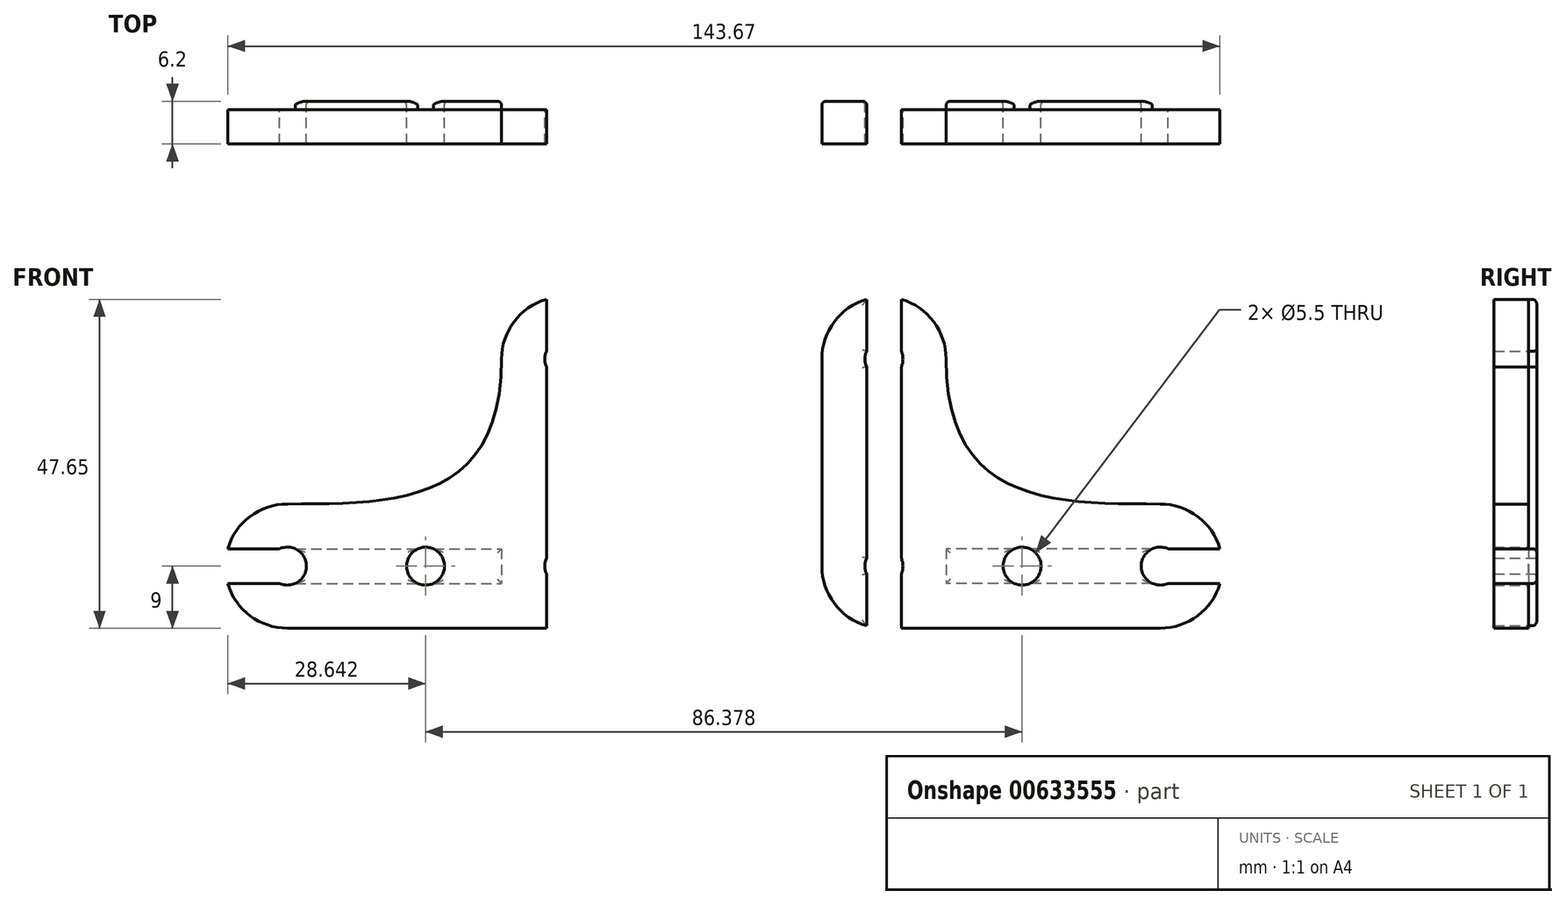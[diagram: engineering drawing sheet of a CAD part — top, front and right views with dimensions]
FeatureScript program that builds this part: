
annotation { "Feature Type Name" : "Feature", "Feature Type Description" : "" }
export const myFeature = defineFeature(function(context is Context, id is Id, definition is map)
    precondition{}
    {
        {
            var Q0;
            Q0=qCreatedBy(makeId("Front.planeOp"),FACE);
            var sketch = newSketch(context, id + "F0", { "sketchPlane" : qUnion([Q0])});
            skLineSegment(sketch, "E0.left", {"start": v(-18, 0) * mm, "end": v(-18, 30) * mm});
            skArc(sketch, "E1", {"start": v(-18, 30) * mm, "mid": v(-9, 39) * mm, "end": v(0, 30) * mm});
            skArc(sketch, "E2", {"start": v(31, 9) * mm, "mid": v(37.36, 6.36) * mm, "end": v(40, 0) * mm});
            skLineSegment(sketch, "E3", {"start": v(0, 30) * mm, "end": v(0, 9) * mm, "construction": true});
            skLineSegment(sketch, "E4", {"start": v(0, 9) * mm, "end": v(31, 9) * mm, "construction": true});
            skLineSegment(sketch, "E5", {"start": v(-18, 39) * mm, "end": v(0, 39) * mm, "construction": true});
            skFitSpline(sketch, "E6", {"points": [v(0, 30) * mm, v(31, 9) * mm], "startDerivative": vector(0, -63) * mm, "endDerivative": vector(46.5, 0) * mm});
            skCircle(sketch, "E7", {"center": v(-9, 30) * mm, "radius": 2.75 * mm});
            skCircle(sketch, "E8", {"center": v(-9, 0) * mm, "radius": 2.75 * mm});
            skCircle(sketch, "E9", {"center": v(31, 0) * mm, "radius": 2.75 * mm});
            skCircle(sketch, "E10", {"center": v(11, 0) * mm, "radius": 2.75 * mm});
            skLineSegment(sketch, "E11.MirrorCS", {"start": v(-18, 0) * mm, "end": v(-18, 0) * mm});
            skArc(sketch, "E12.MirrorCS", {"start": v(31, -9) * mm, "mid": v(37.36, -6.36) * mm, "end": v(40, 0) * mm});
            skCircle(sketch, "E13", {"center": v(-9, 30) * mm, "radius": 2.5 * mm, "construction": true});
            skCircle(sketch, "E14", {"center": v(31, 0) * mm, "radius": 2.5 * mm, "construction": true});
            skLineSegment(sketch, "E15.left", {"start": v(-6.5, 38.65) * mm, "end": v(-6.5, -9) * mm});
            skLineSegment(sketch, "E16.bottom", {"start": v(39.65, 2.5) * mm, "end": v(0, 2.5) * mm});
            skLineSegment(sketch, "E16.top", {"start": v(39.65, -2.5) * mm, "end": v(0, -2.5) * mm});
            skLineSegment(sketch, "E16.right", {"start": v(0, 2.5) * mm, "end": v(0, -2.5) * mm});
            skPoint(sketch, "E16.middle", {"position": v(19.82, 0) * mm});
            skLineSegment(sketch, "E17", {"start": v(31, -9) * mm, "end": v(-9, -9) * mm});
            skPoint(sketch, "E18.orphan", {"position": v(-11.5, -38.65) * mm});
            skPoint(sketch, "E19.orphan", {"position": v(-6.5, -38.65) * mm});
            skArc(sketch, "E20.filletArc", {"start": v(-18, 0) * mm, "mid": v(-15.36, -6.36) * mm, "end": v(-9, -9) * mm});
            skLineSegment(sketch, "E21", {"start": v(-11.5, 38.65) * mm, "end": v(-11.5, -8.65) * mm});
            skLineSegment(sketch, "E22", {"start": v(-32.19, 44.68) * mm, "end": v(-32.19, -13.7) * mm});
            skSolve(sketch);
        }
        {
            var Q0;
            {var subQ0=sQuery(id+"F0.wireOp",EDGE,"E15.right");var subQ1=sQuery(id+"F0.wireOp",EDGE,"E8");var subQ2=makeQuery(id+"F0.imprint","INTERSECT",VERTEX,{"disambiguationData":[OD(1.0)],"derivedFrom":[subQ1,subQ0]});Q0=makeQuery(id+"F0.imprint","IMPRINT",FACE,{"disambiguationData":[TD([[makeQuery(id+"F0.imprint","IMPRINT",EDGE,{"disambiguationData":[TD([[subQ2,-1.0]])],"derivedFrom":subQ1}),-1.0]])]});}
            var Q1;
            {var subQ12=sQuery(id+"F0.wireOp",EDGE,"E0.left");Q1=makeQuery(id+"F0.imprint","IMPRINT",FACE,{"disambiguationData":[TD([[makeQuery(id+"F0.imprint","IMPRINT",EDGE,{"derivedFrom":subQ12}),-1.0]])]});}
            var Q2;
            {var subQ0=sQuery(id+"F0.wireOp",EDGE,"E16.bottom");var subQ1=sQuery(id+"F0.wireOp",EDGE,"E9");var subQ2=makeQuery(id+"F0.imprint","INTERSECT",VERTEX,{"disambiguationData":[OD(0.0)],"derivedFrom":[subQ1,subQ0]});Q2=makeQuery(id+"F0.imprint","IMPRINT",FACE,{"disambiguationData":[TD([[makeQuery(id+"F0.imprint","IMPRINT",EDGE,{"disambiguationData":[TD([[subQ2,-1.0]])],"derivedFrom":subQ1}),-1.0]])]});}
            var Q3;
            {var subQ0=sQuery(id+"F0.wireOp",EDGE,"E15.right");var subQ1=sQuery(id+"F0.wireOp",EDGE,"807e0331-1f37-435d-b5e4-c923ac2277230.MirrorC");var subQ2=makeQuery(id+"F0.imprint","INTERSECT",VERTEX,{"disambiguationData":[OD(0.0)],"derivedFrom":[subQ1,subQ0]});Q3=makeQuery(id+"F0.imprint","IMPRINT",FACE,{"disambiguationData":[TD([[makeQuery(id+"F0.imprint","IMPRINT",EDGE,{"disambiguationData":[TD([[subQ2,1.0]])],"derivedFrom":subQ1}),-1.0]])]});}
            var Q4;
            {var subQ0=sQuery(id+"F0.wireOp",EDGE,"E15.right");var subQ1=sQuery(id+"F0.wireOp",EDGE,"E7");var subQ2=makeQuery(id+"F0.imprint","INTERSECT",VERTEX,{"disambiguationData":[OD(0.0)],"derivedFrom":[subQ1,subQ0]});Q4=makeQuery(id+"F0.imprint","IMPRINT",FACE,{"disambiguationData":[TD([[makeQuery(id+"F0.imprint","IMPRINT",EDGE,{"disambiguationData":[TD([[subQ2,1.0]])],"derivedFrom":subQ1}),1.0]])]});}
            var Q5;
            {var subQ0=sQuery(id+"F0.wireOp",EDGE,"E15.right");var subQ1=sQuery(id+"F0.wireOp",EDGE,"E8");var subQ2=makeQuery(id+"F0.imprint","INTERSECT",VERTEX,{"disambiguationData":[OD(0.0)],"derivedFrom":[subQ1,subQ0]});Q5=makeQuery(id+"F0.imprint","IMPRINT",FACE,{"disambiguationData":[TD([[makeQuery(id+"F0.imprint","IMPRINT",EDGE,{"disambiguationData":[TD([[subQ2,1.0]])],"derivedFrom":subQ1}),1.0]])]});}
            var Q6;
            {var subQ0=sQuery(id+"F0.wireOp",EDGE,"E15.right");var subQ1=sQuery(id+"F0.wireOp",EDGE,"E7");var subQ2=makeQuery(id+"F0.imprint","INTERSECT",VERTEX,{"disambiguationData":[OD(1.0)],"derivedFrom":[subQ1,subQ0]});Q6=makeQuery(id+"F0.imprint","IMPRINT",FACE,{"disambiguationData":[TD([[makeQuery(id+"F0.imprint","IMPRINT",EDGE,{"disambiguationData":[TD([[subQ2,-1.0]])],"derivedFrom":subQ1}),-1.0]])]});}
            var Q7;
            {var subQ5=sQuery(id+"F0.wireOp",EDGE,"E16.right");Q7=makeQuery(id+"F0.imprint","IMPRINT",FACE,{"disambiguationData":[TD([[makeQuery(id+"F0.imprint","IMPRINT",EDGE,{"derivedFrom":subQ5}),1.0]])]});}
            var Q8;
            {var subQ0=sQuery(id+"F0.wireOp",EDGE,"E15.right");var subQ1=sQuery(id+"F0.wireOp",EDGE,"E8");var subQ2=makeQuery(id+"F0.imprint","INTERSECT",VERTEX,{"disambiguationData":[OD(0.0)],"derivedFrom":[subQ1,subQ0]});Q8=makeQuery(id+"F0.imprint","IMPRINT",FACE,{"disambiguationData":[TD([[makeQuery(id+"F0.imprint","IMPRINT",EDGE,{"disambiguationData":[TD([[subQ2,-1.0]])],"derivedFrom":subQ1}),1.0]])]});}
            var Q9;
            {var subQ0=sQuery(id+"F0.wireOp",EDGE,"E15.left");var subQ1=sQuery(id+"F0.wireOp",EDGE,"62d9e975-9eb4-4a92-8864-7b3c9c0b367b0.MirrorCS");var subQ2=makeQuery(id+"F0.imprint","INTERSECT",VERTEX,{"derivedFrom":[subQ1,subQ0]});Q9=makeQuery(id+"F0.imprint","IMPRINT",FACE,{"disambiguationData":[TD([[makeQuery(id+"F0.imprint","IMPRINT",EDGE,{"disambiguationData":[TD([[subQ2,1.0]])],"derivedFrom":subQ1}),1.0]])]});}
            var Q10;
            {var subQ21=sQuery(id+"F0.wireOp",EDGE,"E6");Q10=makeQuery(id+"F0.imprint","IMPRINT",FACE,{"disambiguationData":[TD([[makeQuery(id+"F0.imprint","IMPRINT",EDGE,{"derivedFrom":subQ21}),-1.0]])]});}
            var Q11;
            {var subQ1=sQuery(id+"F0.wireOp",EDGE,"E2");var subQ5=sQuery(id+"F0.wireOp",EDGE,"E12.MirrorCS");var subQ6=makeQuery(id+"F0.imprint","INTERSECT",VERTEX,{"derivedFrom":[subQ1,subQ5]});Q11=makeQuery(id+"F0.imprint","IMPRINT",FACE,{"disambiguationData":[TD([[makeQuery(id+"F0.imprint","IMPRINT",EDGE,{"disambiguationData":[TD([[subQ6,1.0]])],"derivedFrom":subQ1}),-1.0]])]});}
            var Q12;
            {var subQ0=sQuery(id+"F0.wireOp",EDGE,"E15.left");var subQ1=sQuery(id+"F0.wireOp",EDGE,"E1");var subQ2=makeQuery(id+"F0.imprint","INTERSECT",VERTEX,{"derivedFrom":[subQ1,subQ0]});Q12=makeQuery(id+"F0.imprint","IMPRINT",FACE,{"disambiguationData":[TD([[makeQuery(id+"F0.imprint","IMPRINT",EDGE,{"disambiguationData":[TD([[subQ2,1.0]])],"derivedFrom":subQ1}),-1.0]])]});}
            var Q13;
            {var subQ0=sQuery(id+"F0.wireOp",EDGE,"E15.left");var subQ1=sQuery(id+"F0.wireOp",EDGE,"807e0331-1f37-435d-b5e4-c923ac2277230.MirrorC");var subQ2=makeQuery(id+"F0.imprint","INTERSECT",VERTEX,{"disambiguationData":[OD(0.0)],"derivedFrom":[subQ1,subQ0]});Q13=makeQuery(id+"F0.imprint","IMPRINT",FACE,{"disambiguationData":[TD([[makeQuery(id+"F0.imprint","IMPRINT",EDGE,{"disambiguationData":[TD([[subQ2,1.0]])],"derivedFrom":subQ1}),-1.0]])]});}
            var Q14;
            {var subQ0=sQuery(id+"F0.wireOp",EDGE,"E15.right");var subQ1=sQuery(id+"F0.wireOp",EDGE,"E7");var subQ2=makeQuery(id+"F0.imprint","INTERSECT",VERTEX,{"disambiguationData":[OD(0.0)],"derivedFrom":[subQ1,subQ0]});Q14=makeQuery(id+"F0.imprint","IMPRINT",FACE,{"disambiguationData":[TD([[makeQuery(id+"F0.imprint","IMPRINT",EDGE,{"disambiguationData":[TD([[subQ2,-1.0]])],"derivedFrom":subQ1}),1.0]])]});}
            var Q15;
            {var subQ0=sQuery(id+"F0.wireOp",EDGE,"E15.right");var subQ1=sQuery(id+"F0.wireOp",EDGE,"807e0331-1f37-435d-b5e4-c923ac2277230.MirrorC");var subQ2=makeQuery(id+"F0.imprint","INTERSECT",VERTEX,{"disambiguationData":[OD(0.0)],"derivedFrom":[subQ1,subQ0]});Q15=makeQuery(id+"F0.imprint","IMPRINT",FACE,{"disambiguationData":[TD([[makeQuery(id+"F0.imprint","IMPRINT",EDGE,{"disambiguationData":[TD([[subQ2,-1.0]])],"derivedFrom":subQ1}),-1.0]])]});}
            var Q16;
            {var subQ0=sQuery(id+"F0.wireOp",EDGE,"E21");var subQ1=sQuery(id+"F0.wireOp",EDGE,"E7");var subQ2=makeQuery(id+"F0.imprint","INTERSECT",VERTEX,{"disambiguationData":[OD(1.0)],"derivedFrom":[subQ1,subQ0]});Q16=makeQuery(id+"F0.imprint","IMPRINT",FACE,{"disambiguationData":[TD([[makeQuery(id+"F0.imprint","IMPRINT",EDGE,{"disambiguationData":[TD([[subQ2,-1.0]])],"derivedFrom":subQ1}),-1.0]])]});}
            var Q17;
            {var subQ5=sQuery(id+"F0.wireOp",EDGE,"E21");var subQ7=sQuery(id+"F0.wireOp",EDGE,"E8");var subQ9=makeQuery(id+"F0.imprint","INTERSECT",VERTEX,{"disambiguationData":[OD(1.0)],"derivedFrom":[subQ7,subQ5]});Q17=makeQuery(id+"F0.imprint","IMPRINT",FACE,{"disambiguationData":[TD([[makeQuery(id+"F0.imprint","IMPRINT",EDGE,{"disambiguationData":[TD([[subQ9,-1.0]])],"derivedFrom":subQ7}),-1.0]])]});}
            extrude(context, id + "F1", {"entities" : qUnion([Q0, Q1, Q2, Q3, Q4, Q5, Q6, Q7, Q8, Q9, Q10, Q11, Q12, Q13, Q14, Q15, Q16, Q17]), "depth" : 5 * mm, "offsetDistance" : 25 * mm});
        }
        {
            var Q0;
            {var subQ3=sQuery(id+"F0.wireOp",EDGE,"E8");var subQ6=sQuery(id+"F0.wireOp",EDGE,"E15.right");var subQ8=makeQuery(id+"F0.imprint","INTERSECT",VERTEX,{"disambiguationData":[OD(1.0)],"derivedFrom":[subQ3,subQ6]});Q0=makeQuery(id+"F0.imprint","IMPRINT",FACE,{"disambiguationData":[TD([[makeQuery(id+"F0.imprint","IMPRINT",EDGE,{"disambiguationData":[TD([[subQ8,-1.0]])],"derivedFrom":subQ3}),-1.0]])]});}
            var Q1;
            {var subQ3=sQuery(id+"F0.wireOp",EDGE,"E8");var subQ6=sQuery(id+"F0.wireOp",EDGE,"E15.right");var subQ8=makeQuery(id+"F0.imprint","INTERSECT",VERTEX,{"disambiguationData":[OD(0.0)],"derivedFrom":[subQ3,subQ6]});Q1=makeQuery(id+"F0.imprint","IMPRINT",FACE,{"disambiguationData":[TD([[makeQuery(id+"F0.imprint","IMPRINT",EDGE,{"disambiguationData":[TD([[subQ8,1.0]])],"derivedFrom":subQ3}),-1.0]])]});}
            var Q2;
            {var subQ5=sQuery(id+"F0.wireOp",EDGE,"E16.right");Q2=makeQuery(id+"F0.imprint","IMPRINT",FACE,{"disambiguationData":[TD([[makeQuery(id+"F0.imprint","IMPRINT",EDGE,{"derivedFrom":subQ5}),1.0]])]});}
            var Q3;
            {var subQ1=sQuery(id+"F0.wireOp",EDGE,"E16.bottom");var subQ4=sQuery(id+"F0.wireOp",EDGE,"E10");var subQ5=makeQuery(id+"F0.imprint","INTERSECT",VERTEX,{"disambiguationData":[OD(1.0)],"derivedFrom":[subQ4,subQ1]});Q3=makeQuery(id+"F0.imprint","IMPRINT",FACE,{"disambiguationData":[TD([[makeQuery(id+"F0.imprint","IMPRINT",EDGE,{"disambiguationData":[TD([[subQ5,1.0]])],"derivedFrom":subQ4}),-1.0]])]});}
            var Q4;
            {var subQ1=sQuery(id+"F0.wireOp",EDGE,"E2");var subQ5=sQuery(id+"F0.wireOp",EDGE,"E12.MirrorCS");var subQ6=makeQuery(id+"F0.imprint","INTERSECT",VERTEX,{"derivedFrom":[subQ1,subQ5]});Q4=makeQuery(id+"F0.imprint","IMPRINT",FACE,{"disambiguationData":[TD([[makeQuery(id+"F0.imprint","IMPRINT",EDGE,{"disambiguationData":[TD([[subQ6,1.0]])],"derivedFrom":subQ1}),-1.0]])]});}
            var Q5;
            {var subQ0=sQuery(id+"F0.wireOp",EDGE,"E15.left");var subQ1=sQuery(id+"F0.wireOp",EDGE,"E1");var subQ2=makeQuery(id+"F0.imprint","INTERSECT",VERTEX,{"derivedFrom":[subQ1,subQ0]});Q5=makeQuery(id+"F0.imprint","IMPRINT",FACE,{"disambiguationData":[TD([[makeQuery(id+"F0.imprint","IMPRINT",EDGE,{"disambiguationData":[TD([[subQ2,1.0]])],"derivedFrom":subQ1}),-1.0]])]});}
            var Q6;
            {var subQ0=sQuery(id+"F0.wireOp",EDGE,"E15.left");var subQ1=sQuery(id+"F0.wireOp",EDGE,"62d9e975-9eb4-4a92-8864-7b3c9c0b367b0.MirrorCS");var subQ2=makeQuery(id+"F0.imprint","INTERSECT",VERTEX,{"derivedFrom":[subQ1,subQ0]});Q6=makeQuery(id+"F0.imprint","IMPRINT",FACE,{"disambiguationData":[TD([[makeQuery(id+"F0.imprint","IMPRINT",EDGE,{"disambiguationData":[TD([[subQ2,1.0]])],"derivedFrom":subQ1}),1.0]])]});}
            var Q7;
            {var subQ0=sQuery(id+"F0.wireOp",EDGE,"E21");var subQ1=sQuery(id+"F0.wireOp",EDGE,"E7");var subQ2=makeQuery(id+"F0.imprint","INTERSECT",VERTEX,{"disambiguationData":[OD(1.0)],"derivedFrom":[subQ1,subQ0]});Q7=makeQuery(id+"F0.imprint","IMPRINT",FACE,{"disambiguationData":[TD([[makeQuery(id+"F0.imprint","IMPRINT",EDGE,{"disambiguationData":[TD([[subQ2,-1.0]])],"derivedFrom":subQ1}),-1.0]])]});}
            var Q8;
            {var subQ5=sQuery(id+"F0.wireOp",EDGE,"E21");var subQ7=sQuery(id+"F0.wireOp",EDGE,"E8");var subQ9=makeQuery(id+"F0.imprint","INTERSECT",VERTEX,{"disambiguationData":[OD(1.0)],"derivedFrom":[subQ7,subQ5]});Q8=makeQuery(id+"F0.imprint","IMPRINT",FACE,{"disambiguationData":[TD([[makeQuery(id+"F0.imprint","IMPRINT",EDGE,{"disambiguationData":[TD([[subQ9,-1.0]])],"derivedFrom":subQ7}),-1.0]])]});}
            extrude(context, id + "F2", {"entities" : qUnion([Q0, Q1, Q2, Q3, Q4, Q5, Q6, Q7, Q8]), "operationType" : NewBodyOperationType.ADD, "oppositeDirection" : true, "depth" : 1.2 * mm, "offsetDistance" : 25 * mm});
        }
        {
            var Q0;
            Q0=makeQuery(id+"F2.opExtrude","CAP_FACE",FACE,{"disambiguationData":[OSD([sQuery(id+"F0.wireOp",EDGE,"E8"),sQuery(id+"F0.wireOp",EDGE,"807e0331-1f37-435d-b5e4-c923ac2277230.MirrorC"),sQuery(id+"F0.wireOp",EDGE,"E15.left"),sQuery(id+"F0.wireOp",EDGE,"E15.right")])],"isStart":false});
            var Q1;
            Q1=makeQuery(id+"F2.opExtrude","CAP_FACE",FACE,{"disambiguationData":[OSD([sQuery(id+"F0.wireOp",EDGE,"62d9e975-9eb4-4a92-8864-7b3c9c0b367b0.MirrorCS"),sQuery(id+"F0.wireOp",EDGE,"807e0331-1f37-435d-b5e4-c923ac2277230.MirrorC"),sQuery(id+"F0.wireOp",EDGE,"E15.left"),sQuery(id+"F0.wireOp",EDGE,"E15.right")])],"isStart":false});
            var Q2;
            Q2=makeQuery(id+"F2.opExtrude","CAP_FACE",FACE,{"disambiguationData":[OSD([sQuery(id+"F0.wireOp",EDGE,"E7"),sQuery(id+"F0.wireOp",EDGE,"E8"),sQuery(id+"F0.wireOp",EDGE,"E15.left"),sQuery(id+"F0.wireOp",EDGE,"E15.right")])],"isStart":false});
            var Q3;
            Q3=makeQuery(id+"F2.opExtrude","CAP_FACE",FACE,{"disambiguationData":[OSD([sQuery(id+"F0.wireOp",EDGE,"E1"),sQuery(id+"F0.wireOp",EDGE,"E7"),sQuery(id+"F0.wireOp",EDGE,"E15.left"),sQuery(id+"F0.wireOp",EDGE,"E15.right")])],"isStart":false});
            var Q4;
            Q4=makeQuery(id+"F2.opExtrude","CAP_FACE",FACE,{"disambiguationData":[OSD([sQuery(id+"F0.wireOp",EDGE,"E10"),sQuery(id+"F0.wireOp",EDGE,"E16.bottom"),sQuery(id+"F0.wireOp",EDGE,"E16.top"),sQuery(id+"F0.wireOp",EDGE,"E16.right")])],"isStart":false});
            var Q5;
            Q5=makeQuery(id+"F2.opExtrude","CAP_FACE",FACE,{"disambiguationData":[OSD([sQuery(id+"F0.wireOp",EDGE,"E9"),sQuery(id+"F0.wireOp",EDGE,"E10"),sQuery(id+"F0.wireOp",EDGE,"E16.bottom"),sQuery(id+"F0.wireOp",EDGE,"E16.top")])],"isStart":false});
            var Q6;
            Q6=makeQuery(id+"F2.opExtrude","CAP_FACE",FACE,{"disambiguationData":[OSD([sQuery(id+"F0.wireOp",EDGE,"E2"),sQuery(id+"F0.wireOp",EDGE,"E9"),sQuery(id+"F0.wireOp",EDGE,"E12.MirrorCS"),sQuery(id+"F0.wireOp",EDGE,"E16.bottom"),sQuery(id+"F0.wireOp",EDGE,"E16.top")])],"isStart":false});
            var Q7;
            Q7=makeQuery(id+"F2.opExtrude","CAP_FACE",FACE,{"disambiguationData":[OSD([sQuery(id+"F0.wireOp",EDGE,"E8"),sQuery(id+"F0.wireOp",EDGE,"E15.left"),sQuery(id+"F0.wireOp",EDGE,"E17"),sQuery(id+"F0.wireOp",EDGE,"E20.filletArc"),sQuery(id+"F0.wireOp",EDGE,"E21")])],"isStart":false});
            var Q8;
            {var subQ0=sQuery(id+"F0.wireOp",EDGE,"E16.top");Q8=makeQuery(id+"F2.opExtrude","CAP_EDGE",EDGE,{"disambiguationData":[OSD([subQ0]),TDD([makeQuery(id+"F0.imprint","IMPRINT",EDGE,{"disambiguationData":[TD([[makeQuery(id+"F0.imprint","INTERSECT",VERTEX,{"derivedFrom":[subQ0,sQuery(id+"F0.wireOp",EDGE,"E16.right")]}),1.0]])],"derivedFrom":subQ0})])],"isStart":true});}
            var Q9;
            {var subQ0=sQuery(id+"F0.wireOp",EDGE,"E21");Q9=makeQuery(id+"F2.opExtrude","CAP_EDGE",EDGE,{"disambiguationData":[OSD([subQ0]),TDD([makeQuery(id+"F0.imprint","IMPRINT",EDGE,{"disambiguationData":[TD([[makeQuery(id+"F0.imprint","INTERSECT",VERTEX,{"disambiguationData":[OD(1.0)],"derivedFrom":[sQuery(id+"F0.wireOp",EDGE,"E7"),subQ0]}),-1.0]])],"derivedFrom":subQ0})])],"isStart":true});}
            var Q10;
            {var subQ0=sQuery(id+"F0.wireOp",EDGE,"E16.bottom");Q10=makeQuery(id+"F2.opExtrude","CAP_EDGE",EDGE,{"disambiguationData":[OSD([subQ0]),TDD([makeQuery(id+"F0.imprint","IMPRINT",EDGE,{"disambiguationData":[TD([[makeQuery(id+"F0.imprint","INTERSECT",VERTEX,{"derivedFrom":[subQ0,sQuery(id+"F0.wireOp",EDGE,"E16.right")]}),1.0]])],"derivedFrom":subQ0})])],"isStart":true});}
            var Q11;
            {var subQ0=sQuery(id+"F0.wireOp",EDGE,"E15.left");Q11=makeQuery(id+"F2.opExtrude","CAP_EDGE",EDGE,{"disambiguationData":[OSD([subQ0]),TDD([makeQuery(id+"F0.imprint","IMPRINT",EDGE,{"disambiguationData":[TD([[makeQuery(id+"F0.imprint","INTERSECT",VERTEX,{"disambiguationData":[OD(1.0)],"derivedFrom":[sQuery(id+"F0.wireOp",EDGE,"E7"),subQ0]}),-1.0]])],"derivedFrom":subQ0})])],"isStart":true});}
            fillet(context, id + "F3", {"entities" : qUnion([Q0, Q1, Q2, Q3, Q4, Q5, Q6, Q7, Q8, Q9, Q10, Q11]), "radius" : 0.6 * mm, "tangentPropagation" : true, "allowEdgeOverflow" : false});
        }
        {
            var Q0;
            Q0=sQuery(id+"F0.wireOp",EDGE,"E22");
            extrude(context, id + "F4", {"bodyType" : ToolBodyType.SURFACE, "surfaceEntities" : qUnion([Q0]), "depth" : 25 * mm, "offsetDistance" : 25 * mm});
        }
        {
            var Q0;
            Q0=makeQuery(id+"F1.opExtrude","SWEPT_BODY",BODY,{"disambiguationData":[OSD([sQuery(id+"F0.wireOp",EDGE,"E0.left"),sQuery(id+"F0.wireOp",EDGE,"E1"),sQuery(id+"F0.wireOp",EDGE,"E2"),sQuery(id+"F0.wireOp",EDGE,"E6"),sQuery(id+"F0.wireOp",EDGE,"E7"),sQuery(id+"F0.wireOp",EDGE,"E8"),sQuery(id+"F0.wireOp",EDGE,"E9"),sQuery(id+"F0.wireOp",EDGE,"E10"),sQuery(id+"F0.wireOp",EDGE,"E12.MirrorCS"),sQuery(id+"F0.wireOp",EDGE,"E17"),sQuery(id+"F0.wireOp",EDGE,"E20.filletArc")])]});
            var Q1;
            Q1=makeQuery(id+"F4.opExtrude","SWEPT_FACE",FACE,{"disambiguationData":[OSD([sQuery(id+"F0.wireOp",EDGE,"E22")])]});
            mirror(context, id + "F5", {"entities" : qUnion([Q0]), "mirrorPlane" : qUnion([Q1])});
        }
        {
            var Q0;
            Q0=makeQuery(id+"F4.opExtrude","SWEPT_BODY",BODY,{"disambiguationData":[OSD([sQuery(id+"F0.wireOp",EDGE,"E22")])]});
            deleteBodies(context, id + "F6", {"entities" : qUnion([Q0])});
        }
    });
